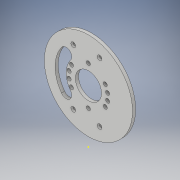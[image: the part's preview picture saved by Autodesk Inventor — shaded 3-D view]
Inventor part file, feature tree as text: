
AUTODESK INVENTOR PART (.ipt)
format: ipt  version: 2019 (Build 230136000, 136)  size: 308,736 bytes
history: native  units: in
note: dims shown in document units (in); Inventor stores cm internally (conversion verified against a paired STEP export)
features: sketch x10, move_body x10, extrude x7, direct_edit x4, hole x2, imported_body x1
ambient origin geometry x8: Origin, YZ Plane, XZ Plane, XY Plane, X Axis, Y Axis, Z Axis, Center Point
bodies: Solid1 (feature_tree)
feature tree (34):
  imported_body  "Imported1"
  extrude  "Extrusion1"  Depth=0.237in TaperAngle=0.0deg
  extrude  "Extrusion2"  Depth=11.5in
  direct_edit  "Direct Edit1"
  hole  "Hole1"  [1 undecoded]
  hole  "Hole5"  [1 undecoded]
  extrude  "Extrusion3"  TaperAngle=0.0deg  [1 undecoded]
  extrude  "Extrusion4"  Depth=0.24in TaperAngle=0.0deg
  direct_edit  "Direct Edit2"
  extrude  "Extrusion5"  TaperAngle=0.0deg  [1 undecoded]
  direct_edit  "Direct Edit3"
  extrude  "Extrusion6"  TaperAngle=0.0deg  [1 undecoded]
  direct_edit  "Direct Edit4"
  sketch  "Sketch21"  dims[d113=0.0in d114=0.0in d115=-0.013in d118=0.0in d119=0.0in d120=0.01in]
  extrude  "Extrusion9"  Depth=0.01in TaperAngle=0.0deg
  sketch  "Sketch1"  dims[d0=1.0in d1=0.0in d2=0.237in d3=0.0in]
  sketch  "Sketch2"  dims[d4=0.0in d5=0.0in d6=0.0008in d7=11.5in]
  sketch  "Sketch4"  dims[d8=0.65in d9=0.75in d10=0.375in d11=0.25in d12=0.5635in d13=1.0in d14=0.8108in d15=4.205in]
  sketch  "Sketch8"  dims[d54=0.196in d55=0.5in d56=0.375in d57=0.25in d58=0.5635in d59=0.75in d60=0.0in d90=1.0in d91=0.0in]
  sketch  "Sketch14"  dims[d92=0.24in d93=0.0in d94=0.0in d95=0.0in d96=-0.003in]
  sketch  "Sketch15"  dims[d97=0.0in d98=0.0in d99=-0.003in d100=0.24in d101=0.0in]
  sketch  "Sketch16"  dims[d102=0.0in d103=0.0in d104=-0.003in d105=0.0in d106=0.0in d107=-0.003in]
  sketch  "Sketch17"  dims[d108=0.25in d109=0.0in d110=0.0in d111=0.0in d112=-0.013in]
  sketch  "Sketch22"  dims[d123=0.0in d124=0.0in d125=0.01in d126=0.0in d127=0.0in d128=0.01in d129=5.0in d130=0.1956in d131=0.1413in d132=0.1956in d133=0.1413in d139=1.0in d140=0.0in d28=1.0in d29=1.0in d30=1.0in d31=0.15in d32=0.25in d33=0.375in d34=32.2835in d35=0.75in d36=46.4567in d37=0.0625in d38=0.75in d39=0.375in]
  move_body  "Move1"
  move_body  "Move2"
  move_body  "Move3"
  move_body  "Move4"
  move_body  "Move5"
  move_body  "Move6"
  move_body  "Move7"
  move_body  "Move8"
  move_body  "Move9"
  move_body  "Move10"
note: 5 required parameter values undecoded (feature->parameter linkage not recoverable at this tier; creation-order binding heuristic only, values carry confidence <= 0.55)
